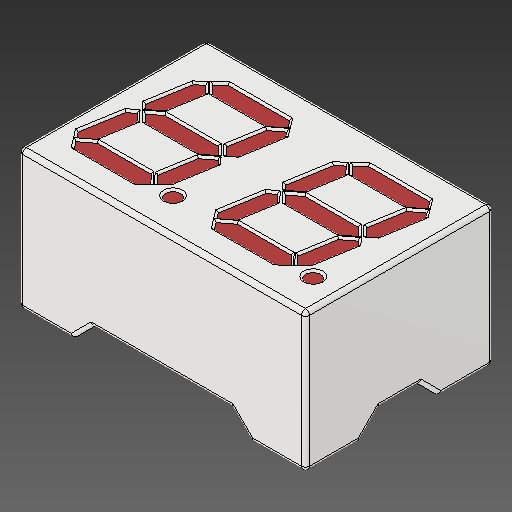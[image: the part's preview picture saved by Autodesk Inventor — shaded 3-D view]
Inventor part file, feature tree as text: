
AUTODESK INVENTOR PART (.ipt)
format: ipt  version: 2018.2 (Build 222227000, 227)  size: 238,592 bytes
history: native  units: mm
features: other x1, fillet x1
ambient origin geometry x8: Origin, YZ Plane, XZ Plane, XY Plane, X Axis, Y Axis, Z Axis, Center Point
bodies: Body1 (feature_tree)
feature tree (2):
  other  "ソリッド1"
  fillet  "Fillet2"  [1 undecoded]
note: 1 required parameter value undecoded (feature->parameter linkage not recoverable at this tier; creation-order binding heuristic only, values carry confidence <= 0.55)
